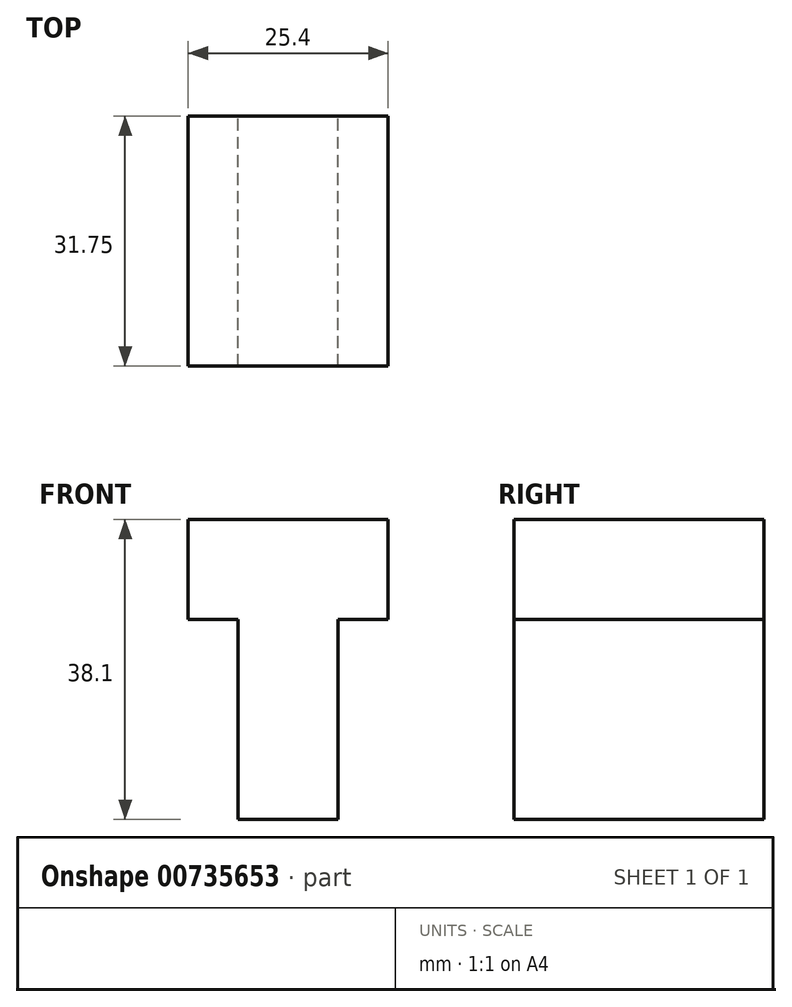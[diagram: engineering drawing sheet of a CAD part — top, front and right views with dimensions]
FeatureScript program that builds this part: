
annotation { "Feature Type Name" : "Feature", "Feature Type Description" : "" }
export const myFeature = defineFeature(function(context is Context, id is Id, definition is map)
    precondition{}
    {
        {
            var Q0;
            Q0=qCreatedBy(makeId("Front.planeOp"),FACE);
            var sketch = newSketch(context, id + "F0", { "sketchPlane" : qUnion([Q0])});
            skLineSegment(sketch, "E0", {"start": v(0, 0) * mm, "end": v(12.7, 0) * mm});
            skLineSegment(sketch, "E1", {"start": v(12.7, 0) * mm, "end": v(12.7, 25.4) * mm});
            skLineSegment(sketch, "E2", {"start": v(12.7, 25.4) * mm, "end": v(19.05, 25.4) * mm});
            skLineSegment(sketch, "E3", {"start": v(19.05, 25.4) * mm, "end": v(19.05, 38.1) * mm});
            skLineSegment(sketch, "E4", {"start": v(19.05, 38.1) * mm, "end": v(-6.35, 38.1) * mm});
            skLineSegment(sketch, "E5", {"start": v(-6.35, 38.1) * mm, "end": v(-6.35, 25.4) * mm});
            skLineSegment(sketch, "E6", {"start": v(-6.35, 25.4) * mm, "end": v(0, 25.4) * mm});
            skLineSegment(sketch, "E7", {"start": v(0, 25.4) * mm, "end": v(0, 0) * mm});
            skSolve(sketch);
        }
        {
            var Q0;
            Q0=makeQuery(id+"F0.imprint","IMPRINT",FACE,{"disambiguationData":[TD([[makeQuery(id+"F0.imprint","IMPRINT",EDGE,{"derivedFrom":sQuery(id+"F0.wireOp",EDGE,"E0")}),1.0]])]});
            extrude(context, id + "F1", {"entities" : qUnion([Q0]), "depth" : 31.75 * mm, "offsetDistance" : 25.4 * mm});
        }
    });
